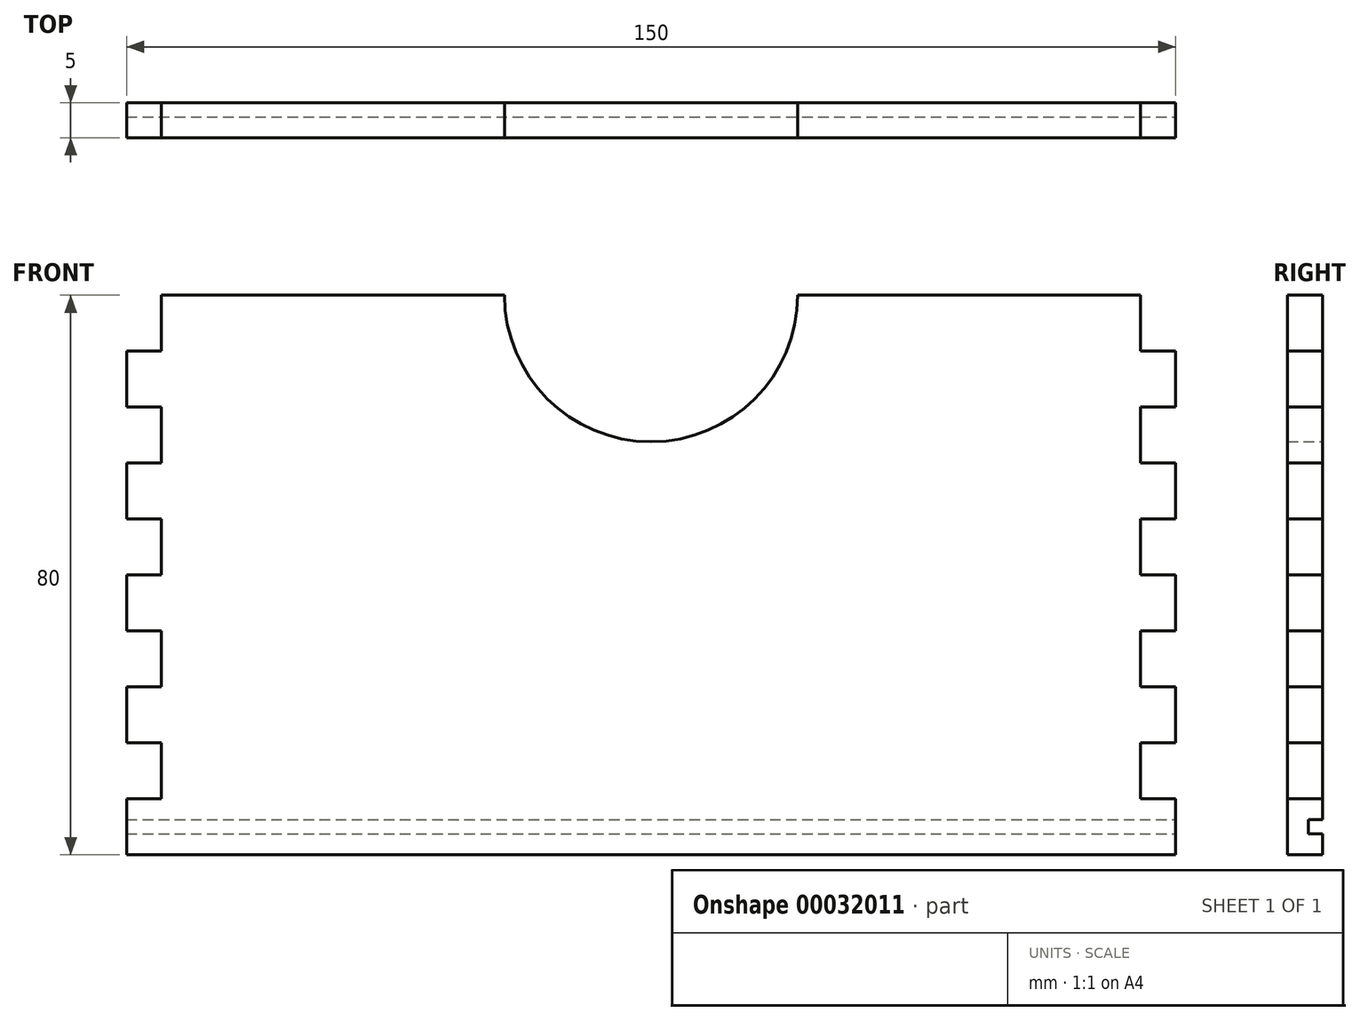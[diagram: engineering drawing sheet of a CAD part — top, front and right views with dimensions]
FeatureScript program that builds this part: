
annotation { "Feature Type Name" : "Feature", "Feature Type Description" : "" }
export const myFeature = defineFeature(function(context is Context, id is Id, definition is map)
    precondition{}
    {
        {
            assignVariable(context, id + "F0", {"name" : "ep", "anyValue" : 5});
        }
        {
            var Q0;
            Q0=qCreatedBy(makeId("Front.planeOp"),FACE);
            var sketch = newSketch(context, id + "F1", { "sketchPlane" : qUnion([Q0])});
            skArc(sketch, "E0", {"start": v(-20.96, 0) * mm, "mid": v(0, -20.96) * mm, "end": v(20.96, 0) * mm});
            skLineSegment(sketch, "E1", {"start": v(20.96, 0) * mm, "end": v(70, 0) * mm});
            skLineSegment(sketch, "E2", {"start": v(70, 0) * mm, "end": v(70, -8) * mm});
            skLineSegment(sketch, "E3", {"start": v(70, -8) * mm, "end": v(75, -8) * mm});
            skLineSegment(sketch, "E4", {"start": v(75, -8) * mm, "end": v(75, -16) * mm});
            skLineSegment(sketch, "E5", {"start": v(75, -16) * mm, "end": v(70, -16) * mm});
            skLineSegment(sketch, "E6", {"start": v(70, -16) * mm, "end": v(70, -24) * mm});
            skLineSegment(sketch, "E7", {"start": v(70, -24) * mm, "end": v(75, -24) * mm});
            skLineSegment(sketch, "E8", {"start": v(75, -24) * mm, "end": v(75, -32) * mm});
            skLineSegment(sketch, "E9", {"start": v(75, -32) * mm, "end": v(70, -32) * mm});
            skLineSegment(sketch, "E10", {"start": v(70, -32) * mm, "end": v(70, -40) * mm});
            skLineSegment(sketch, "E11", {"start": v(70, -40) * mm, "end": v(75, -40) * mm});
            skLineSegment(sketch, "E12", {"start": v(75, -40) * mm, "end": v(75, -48) * mm});
            skLineSegment(sketch, "E13", {"start": v(75, -48) * mm, "end": v(70, -48) * mm});
            skLineSegment(sketch, "E14", {"start": v(70, -48) * mm, "end": v(70, -56) * mm});
            skLineSegment(sketch, "E15", {"start": v(70, -56) * mm, "end": v(75, -56) * mm});
            skLineSegment(sketch, "E16", {"start": v(75, -56) * mm, "end": v(75, -64) * mm});
            skLineSegment(sketch, "E17", {"start": v(75, -64) * mm, "end": v(70, -64) * mm});
            skLineSegment(sketch, "E18", {"start": v(70, -64) * mm, "end": v(70, -72) * mm});
            skLineSegment(sketch, "E19", {"start": v(70, -72) * mm, "end": v(75, -72) * mm});
            skLineSegment(sketch, "E20", {"start": v(75, -72) * mm, "end": v(75, -80) * mm});
            skLineSegment(sketch, "E21.MirrorCS", {"start": v(-70, -56) * mm, "end": v(-75, -56) * mm});
            skLineSegment(sketch, "E22.MirrorCS", {"start": v(-75, -48) * mm, "end": v(-70, -48) * mm});
            skLineSegment(sketch, "E23.MirrorCS", {"start": v(-70, -8) * mm, "end": v(-75, -8) * mm});
            skLineSegment(sketch, "E24.MirrorCS", {"start": v(-75, -64) * mm, "end": v(-70, -64) * mm});
            skLineSegment(sketch, "E25.MirrorCS", {"start": v(-75, -16) * mm, "end": v(-70, -16) * mm});
            skLineSegment(sketch, "E26.MirrorCS", {"start": v(-70, -24) * mm, "end": v(-75, -24) * mm});
            skLineSegment(sketch, "E27.MirrorCS", {"start": v(-70, -40) * mm, "end": v(-75, -40) * mm});
            skLineSegment(sketch, "E28.MirrorCS", {"start": v(-75, -32) * mm, "end": v(-70, -32) * mm});
            skLineSegment(sketch, "E29.MirrorCS", {"start": v(-70, -72) * mm, "end": v(-75, -72) * mm});
            skLineSegment(sketch, "E30.MirrorCS", {"start": v(-70, -48) * mm, "end": v(-70, -56) * mm});
            skLineSegment(sketch, "E31.MirrorCS", {"start": v(-20.96, 0) * mm, "end": v(-70, 0) * mm});
            skLineSegment(sketch, "E32.MirrorCS", {"start": v(-75, -56) * mm, "end": v(-75, -64) * mm});
            skLineSegment(sketch, "E33.MirrorCS", {"start": v(-70, 0) * mm, "end": v(-70, -8) * mm});
            skLineSegment(sketch, "E34.MirrorCS", {"start": v(-70, -64) * mm, "end": v(-70, -72) * mm});
            skLineSegment(sketch, "E35.MirrorCS", {"start": v(-75, -8) * mm, "end": v(-75, -16) * mm});
            skLineSegment(sketch, "E36.MirrorCS", {"start": v(-75, -72) * mm, "end": v(-75, -80) * mm});
            skLineSegment(sketch, "E37.MirrorCS", {"start": v(-70, -32) * mm, "end": v(-70, -40) * mm});
            skLineSegment(sketch, "E38.MirrorCS", {"start": v(-70, -16) * mm, "end": v(-70, -24) * mm});
            skLineSegment(sketch, "E39.MirrorCS", {"start": v(-75, -40) * mm, "end": v(-75, -48) * mm});
            skLineSegment(sketch, "E40.MirrorCS", {"start": v(-75, -24) * mm, "end": v(-75, -32) * mm});
            skLineSegment(sketch, "E41.MirrorCS", {"start": v(-75, -80) * mm, "end": v(75, -80) * mm});
            skSolve(sketch);
        }
        {
            var Q0;
            Q0=makeQuery(id+"F1.imprint","IMPRINT",FACE,{"disambiguationData":[TD([[makeQuery(id+"F1.imprint","IMPRINT",EDGE,{"derivedFrom":sQuery(id+"F1.wireOp",EDGE,"E0")}),-1.0]])]});
            extrude(context, id + "F2", {"entities" : qUnion([Q0]), "depth" : (getVariable(context, 'ep')) * mm});
        }
        {
            var Q0;
            Q0=makeQuery(id+"F2.opExtrude","SWEPT_FACE",FACE,{"disambiguationData":[OSD([sQuery(id+"F1.wireOp",EDGE,"E20")])]});
            var sketch = newSketch(context, id + "F3", { "sketchPlane" : qUnion([Q0])});
            skLineSegment(sketch, "E42", {"start": v(0, -75) * mm, "end": v(-2, -75) * mm});
            skLineSegment(sketch, "E43", {"start": v(-2, -75) * mm, "end": v(-2, -77) * mm});
            skLineSegment(sketch, "E44", {"start": v(-2, -77) * mm, "end": v(0, -77) * mm});
            skLineSegment(sketch, "E45", {"start": v(0, -77) * mm, "end": v(0, -75) * mm});
            skSolve(sketch);
        }
        {
            var Q0;
            Q0=makeQuery(id+"F3.imprint","IMPRINT",FACE,{"disambiguationData":[TD([[makeQuery(id+"F3.imprint","IMPRINT",EDGE,{"derivedFrom":sQuery(id+"F3.wireOp",EDGE,"E42")}),1.0]])]});
            extrude(context, id + "F4", {"entities" : qUnion([Q0]), "operationType" : NewBodyOperationType.REMOVE, "endBound" : BoundingType.THROUGH_ALL, "oppositeDirection" : true, "depth" : 25 * mm});
        }
    });
